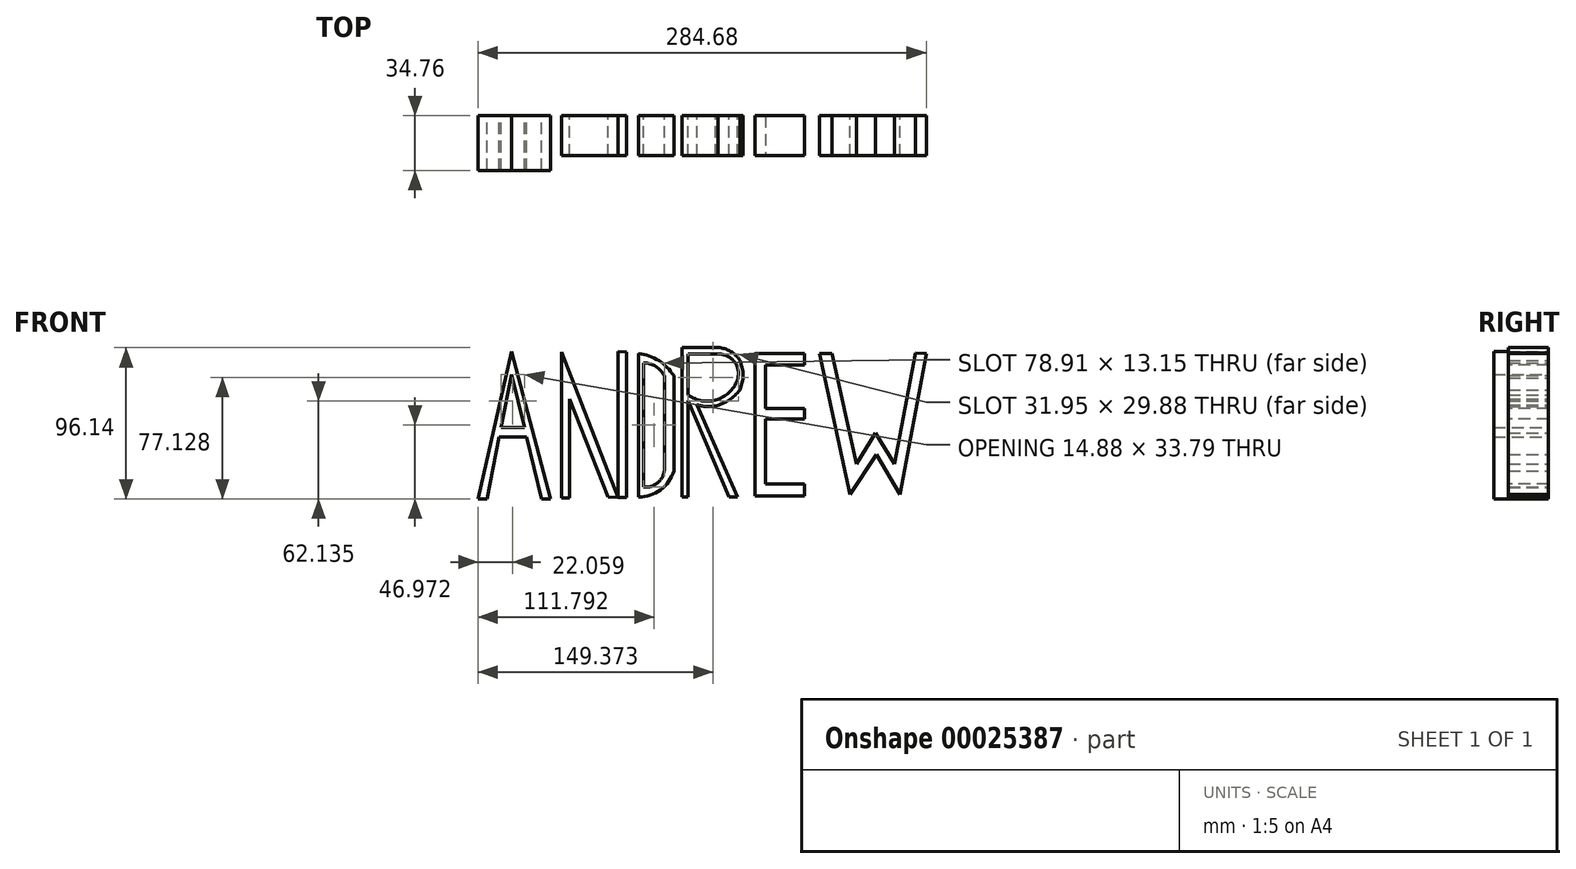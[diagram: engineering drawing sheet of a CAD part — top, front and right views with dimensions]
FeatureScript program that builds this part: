
annotation { "Feature Type Name" : "Feature", "Feature Type Description" : "" }
export const myFeature = defineFeature(function(context is Context, id is Id, definition is map)
    precondition{}
    {
        {
            var Q0;
            Q0=qCreatedBy(makeId("Front.planeOp"),FACE);
            var sketch = newSketch(context, id + "F0", { "sketchPlane" : qUnion([Q0])});
            skLineSegment(sketch, "E0", {"start": v(-75.47, -35.86) * mm, "end": v(-35.39, 55.58) * mm});
            skLineSegment(sketch, "E1", {"start": v(-68.9, -35.86) * mm, "end": v(-75.47, -35.86) * mm});
            skLineSegment(sketch, "E2", {"start": v(-68.9, -35.86) * mm, "end": v(-36.05, 39.07) * mm});
            skLineSegment(sketch, "E3", {"start": v(-36.05, 39.07) * mm, "end": v(-9.08, -38.99) * mm});
            skLineSegment(sketch, "E4", {"start": v(-9.08, -38.99) * mm, "end": v(-3.44, -38.99) * mm});
            skLineSegment(sketch, "E5", {"start": v(-3.44, -38.99) * mm, "end": v(-35.39, 55.58) * mm});
            skLineSegment(sketch, "E6", {"start": v(-53.18, 0) * mm, "end": v(-22.55, 0) * mm});
            skLineSegment(sketch, "E7", {"start": v(-49.54, 8.29) * mm, "end": v(-25.41, 8.29) * mm});
            skSolve(sketch);
        }
        {
            var Q0;
            {var subQ1=sQuery(id+"F0.wireOp",EDGE,"E6");Q0=makeQuery(id+"F0.imprint","IMPRINT",FACE,{"disambiguationData":[TD([[makeQuery(id+"F0.imprint","IMPRINT",EDGE,{"derivedFrom":subQ1}),1.0]])]});}
            var Q1;
            Q1=makeQuery(id+"F0.imprint","IMPRINT",FACE,{"disambiguationData":[TD([[makeQuery(id+"F0.imprint","IMPRINT",EDGE,{"derivedFrom":sQuery(id+"F0.wireOp",EDGE,"E0")}),-1.0]])]});
            extrude(context, id + "F1", {"entities" : qUnion([Q0, Q1]), "depth" : 25.4 * mm});
        }
        {
            var Q0;
            Q0=makeQuery(id+"F1.opExtrude","CAP_FACE",FACE,{"disambiguationData":[OSD([sQuery(id+"F0.wireOp",EDGE,"E0"),sQuery(id+"F0.wireOp",EDGE,"E1"),sQuery(id+"F0.wireOp",EDGE,"E2"),sQuery(id+"F0.wireOp",EDGE,"E3"),sQuery(id+"F0.wireOp",EDGE,"E4"),sQuery(id+"F0.wireOp",EDGE,"E5"),sQuery(id+"F0.wireOp",EDGE,"E6"),sQuery(id+"F0.wireOp",EDGE,"E7")])],"isStart":false});
            var sketch = newSketch(context, id + "F2", { "sketchPlane" : qUnion([Q0])});
            skSolve(sketch);
        }
        {
            var Q0;
            Q0 = qSketchRegion(id + "FRlJwE8yTnHYSPP_1", true);
            var Q1;
            Q1=makeQuery(id+"F2.imprint","IMPRINT",FACE,{"disambiguationData":[TD([[makeQuery(id+"F2.imprint","IMPRINT",EDGE,{"derivedFrom":makeQuery(id+"F1.opExtrude","CAP_EDGE",EDGE,{"disambiguationData":[OSD([sQuery(id+"F0.wireOp",EDGE,"E0")])],"isStart":false})}),-1.0]])]});
            extrude(context, id + "F3", {"entities" : qUnion([Q0, Q1]), "operationType" : NewBodyOperationType.ADD, "depth" : 25.4 * mm});
        }
        {
            var Q0;
            Q0=makeQuery(id+"F1.opExtrude","SWEPT_BODY",BODY,{"disambiguationData":[OSD([sQuery(id+"F0.wireOp",EDGE,"E0"),sQuery(id+"F0.wireOp",EDGE,"E1"),sQuery(id+"F0.wireOp",EDGE,"E2"),sQuery(id+"F0.wireOp",EDGE,"E3"),sQuery(id+"F0.wireOp",EDGE,"E4"),sQuery(id+"F0.wireOp",EDGE,"E5"),sQuery(id+"F0.wireOp",EDGE,"E6"),sQuery(id+"F0.wireOp",EDGE,"E7")])]});
            deleteBodies(context, id + "F4", {"entities" : qUnion([Q0])});
        }
        {
            var Q0;
            Q0=qCreatedBy(makeId("Front.planeOp"),FACE);
            var sketch = newSketch(context, id + "F5", { "sketchPlane" : qUnion([Q0])});
            skLineSegment(sketch, "E8", {"start": v(-74.84, -28.34) * mm, "end": v(-69.2, -28.34) * mm});
            skLineSegment(sketch, "E9", {"start": v(-74.84, -28.34) * mm, "end": v(-53.52, 65.43) * mm});
            skLineSegment(sketch, "E10", {"start": v(-53.52, 65.43) * mm, "end": v(-28.74, -28.34) * mm});
            skLineSegment(sketch, "E11", {"start": v(-69.2, -28.34) * mm, "end": v(-61.36, 11.17) * mm});
            skLineSegment(sketch, "E12", {"start": v(-53.52, 50.69) * mm, "end": v(-45.34, 16.9) * mm});
            skLineSegment(sketch, "E13", {"start": v(-61.36, 11.17) * mm, "end": v(-43.95, 11.17) * mm});
            skLineSegment(sketch, "E14", {"start": v(-60.22, 16.9) * mm, "end": v(-45.34, 16.9) * mm});
            skLineSegment(sketch, "E15.trimOffspring", {"start": v(-34.39, -28.34) * mm, "end": v(-28.74, -28.34) * mm});
            skLineSegment(sketch, "E16.trimOffspring", {"start": v(-60.22, 16.9) * mm, "end": v(-53.52, 50.69) * mm});
            skLineSegment(sketch, "E17.trimOffspring", {"start": v(-43.95, 11.17) * mm, "end": v(-34.39, -28.34) * mm});
            skSolve(sketch);
        }
        {
            var Q0;
            Q0=makeQuery(id+"F5.imprint","IMPRINT",FACE,{"disambiguationData":[TD([[makeQuery(id+"F5.imprint","IMPRINT",EDGE,{"derivedFrom":sQuery(id+"F5.wireOp",EDGE,"E8")}),1.0]])]});
            extrude(context, id + "F6", {"entities" : qUnion([Q0]), "depth" : 9.36 * mm});
        }
        {
            var Q0;
            Q0=qCreatedBy(makeId("Front.planeOp"),FACE);
            var sketch = newSketch(context, id + "F7", { "sketchPlane" : qUnion([Q0])});
            skLineSegment(sketch, "E18", {"start": v(-21.92, -27.71) * mm, "end": v(-21.92, 64.98) * mm});
            skLineSegment(sketch, "E19", {"start": v(-21.92, 64.98) * mm, "end": v(14.1, -27.4) * mm});
            skLineSegment(sketch, "E20", {"start": v(14.1, -27.4) * mm, "end": v(14.1, 65.3) * mm});
            skLineSegment(sketch, "E21", {"start": v(-21.92, -27.71) * mm, "end": v(-16.6, -27.71) * mm});
            skLineSegment(sketch, "E22", {"start": v(-16.6, -27.71) * mm, "end": v(-16.6, 35.23) * mm});
            skLineSegment(sketch, "E23", {"start": v(-16.6, 35.23) * mm, "end": v(7.73, -27.18) * mm});
            skLineSegment(sketch, "E24", {"start": v(7.73, -27.18) * mm, "end": v(14.1, -27.4) * mm});
            skLineSegment(sketch, "E25", {"start": v(14.1, -27.4) * mm, "end": v(19.42, -27.4) * mm});
            skLineSegment(sketch, "E26", {"start": v(19.42, -27.4) * mm, "end": v(19.42, 64.98) * mm});
            skLineSegment(sketch, "E27", {"start": v(19.42, 64.98) * mm, "end": v(14.1, 65.3) * mm});
            skSolve(sketch);
        }
        {
            var Q0;
            Q0=makeQuery(id+"F7.imprint","IMPRINT",FACE,{"disambiguationData":[TD([[makeQuery(id+"F7.imprint","IMPRINT",EDGE,{"derivedFrom":sQuery(id+"F7.wireOp",EDGE,"E20")}),-1.0]])]});
            var Q1;
            Q1=makeQuery(id+"F7.imprint","IMPRINT",FACE,{"disambiguationData":[TD([[makeQuery(id+"F7.imprint","IMPRINT",EDGE,{"derivedFrom":sQuery(id+"F7.wireOp",EDGE,"E18")}),-1.0]])]});
            extrude(context, id + "F8", {"entities" : qUnion([Q0, Q1]), "depth" : 25.4 * mm});
        }
        {
            var Q0;
            Q0=makeQuery(id+"F6.opExtrude","CAP_FACE",FACE,{"disambiguationData":[OSD([sQuery(id+"F5.wireOp",EDGE,"E8"),sQuery(id+"F5.wireOp",EDGE,"E9"),sQuery(id+"F5.wireOp",EDGE,"E10"),sQuery(id+"F5.wireOp",EDGE,"E11"),sQuery(id+"F5.wireOp",EDGE,"E12"),sQuery(id+"F5.wireOp",EDGE,"E13"),sQuery(id+"F5.wireOp",EDGE,"E14"),sQuery(id+"F5.wireOp",EDGE,"E15.trimOffspring"),sQuery(id+"F5.wireOp",EDGE,"E16.trimOffspring"),sQuery(id+"F5.wireOp",EDGE,"E17.trimOffspring")])],"isStart":false});
            extrude(context, id + "F9", {"entities" : qUnion([Q0]), "operationType" : NewBodyOperationType.ADD, "depth" : 25.4 * mm});
        }
        {
            var Q0;
            Q0=qCreatedBy(makeId("Front.planeOp"),FACE);
            var sketch = newSketch(context, id + "F10", { "sketchPlane" : qUnion([Q0])});
            skLineSegment(sketch, "E28", {"start": v(19.1, -27.09) * mm, "end": v(27.24, -27.09) * mm});
            skLineSegment(sketch, "E29", {"start": v(27.24, -27.09) * mm, "end": v(27.24, 64.04) * mm});
            skArc(sketch, "E30", {"start": v(49.48, 49.95) * mm, "mid": v(39.96, 59.52) * mm, "end": v(27.24, 64.04) * mm});
            skLineSegment(sketch, "E31", {"start": v(49.48, 49.95) * mm, "end": v(49.48, -10.5) * mm});
            skArc(sketch, "E32", {"start": v(27.24, -27.09) * mm, "mid": v(41.12, -22.48) * mm, "end": v(49.48, -10.5) * mm});
            skArc(sketch, "E33", {"start": v(43.53, 49.95) * mm, "mid": v(38.07, 55.83) * mm, "end": v(30.38, 58.09) * mm});
            skLineSegment(sketch, "E34", {"start": v(43.53, 49.95) * mm, "end": v(43.53, -8.92) * mm});
            skLineSegment(sketch, "E35", {"start": v(30.38, 58.09) * mm, "end": v(30.38, -8.92) * mm});
            skArc(sketch, "E36", {"start": v(30.38, -20.82) * mm, "mid": v(39.6, -17.8) * mm, "end": v(43.53, -8.92) * mm});
            skLineSegment(sketch, "E37", {"start": v(30.38, -20.82) * mm, "end": v(30.38, -8.92) * mm});
            skSolve(sketch);
        }
        {
            var Q0;
            Q0 = qSketchRegion(id + "F10", true);
            extrude(context, id + "F11", {"entities" : qUnion([Q0]), "depth" : 25.4 * mm});
        }
        {
            var Q0;
            Q0=qCreatedBy(makeId("Front.planeOp"),FACE);
            var sketch = newSketch(context, id + "F12", { "sketchPlane" : qUnion([Q0])});
            skLineSegment(sketch, "E38", {"start": v(58.56, -27.09) * mm, "end": v(58.56, 61.53) * mm});
            skLineSegment(sketch, "E39", {"start": v(58.56, 63.73) * mm, "end": v(58.56, 61.53) * mm});
            skLineSegment(sketch, "E40", {"start": v(58.56, 63.73) * mm, "end": v(77.97, 63.73) * mm});
            skArc(sketch, "E41", {"start": v(90.19, 48.38) * mm, "mid": v(87.78, 59) * mm, "end": v(77.97, 63.73) * mm});
            skArc(sketch, "E42", {"start": v(58.56, 37.73) * mm, "mid": v(77.14, 34.84) * mm, "end": v(90.19, 48.38) * mm});
            skArc(sketch, "E43", {"start": v(91.44, 59.66) * mm, "mid": v(85.55, 65.41) * mm, "end": v(77.66, 67.8) * mm});
            skArc(sketch, "E44", {"start": v(91.44, 40.87) * mm, "mid": v(93.42, 50.26) * mm, "end": v(91.44, 59.66) * mm});
            skArc(sketch, "E45", {"start": v(76.1, 30.85) * mm, "mid": v(84.63, 34.53) * mm, "end": v(91.44, 40.87) * mm});
            skArc(sketch, "E46", {"start": v(58.56, 34.3) * mm, "mid": v(66.97, 30.75) * mm, "end": v(76.1, 30.85) * mm});
            skLineSegment(sketch, "E47", {"start": v(77.66, 67.8) * mm, "end": v(58.56, 67.8) * mm});
            skLineSegment(sketch, "E48", {"start": v(58.56, 67.8) * mm, "end": v(58.56, 63.73) * mm});
            skLineSegment(sketch, "E49", {"start": v(58.56, 67.8) * mm, "end": v(54.8, 67.8) * mm});
            skLineSegment(sketch, "E50", {"start": v(54.8, 67.8) * mm, "end": v(54.8, -27.09) * mm});
            skLineSegment(sketch, "E51", {"start": v(54.8, -27.09) * mm, "end": v(58.56, -27.09) * mm});
            skLineSegment(sketch, "E52", {"start": v(58.56, 34.3) * mm, "end": v(84.55, -27.09) * mm});
            skLineSegment(sketch, "E53", {"start": v(84.55, -27.09) * mm, "end": v(89.87, -27.09) * mm});
            skLineSegment(sketch, "E54", {"start": v(89.87, -27.09) * mm, "end": v(64.16, 31.5) * mm});
            skSolve(sketch);
        }
        {
            var Q0;
            Q0 = qSketchRegion(id + "F12", true);
            extrude(context, id + "F13", {"entities" : qUnion([Q0]), "depth" : 25.4 * mm});
        }
        {
            var Q0;
            Q0=makeQuery(id+"F11.opExtrude","CAP_FACE",FACE,{"disambiguationData":[OSD([sQuery(id+"F10.wireOp",EDGE,"E29"),sQuery(id+"F10.wireOp",EDGE,"E30"),sQuery(id+"F10.wireOp",EDGE,"E31"),sQuery(id+"F10.wireOp",EDGE,"E32"),sQuery(id+"F10.wireOp",EDGE,"E33"),sQuery(id+"F10.wireOp",EDGE,"E34"),sQuery(id+"F10.wireOp",EDGE,"E35"),sQuery(id+"F10.wireOp",EDGE,"E36"),sQuery(id+"F10.wireOp",EDGE,"E37")])],"isStart":false});
            var sketch = newSketch(context, id + "F14", { "sketchPlane" : qUnion([Q0])});
            skLineSegment(sketch, "E55", {"start": v(132.62, 64.04) * mm, "end": v(101, 64.1) * mm});
            skLineSegment(sketch, "E56", {"start": v(101, 64.1) * mm, "end": v(101, -26.46) * mm});
            skLineSegment(sketch, "E57", {"start": v(132.62, 64.04) * mm, "end": v(132.62, 56.84) * mm});
            skLineSegment(sketch, "E58", {"start": v(132.62, 56.84) * mm, "end": v(107.88, 56.84) * mm});
            skLineSegment(sketch, "E59", {"start": v(107.88, 56.84) * mm, "end": v(107.88, 29.28) * mm});
            skLineSegment(sketch, "E60", {"start": v(107.88, 29.28) * mm, "end": v(132.62, 29.28) * mm});
            skLineSegment(sketch, "E61", {"start": v(132.62, 29.28) * mm, "end": v(132.62, 22.4) * mm});
            skLineSegment(sketch, "E62", {"start": v(132.62, 22.4) * mm, "end": v(107.88, 22.4) * mm});
            skLineSegment(sketch, "E63", {"start": v(107.88, 22.4) * mm, "end": v(107.88, -18.95) * mm});
            skLineSegment(sketch, "E64", {"start": v(107.88, -18.95) * mm, "end": v(132.62, -18.95) * mm});
            skLineSegment(sketch, "E65", {"start": v(132.62, -18.95) * mm, "end": v(132.62, -26.46) * mm});
            skLineSegment(sketch, "E66", {"start": v(132.62, -26.46) * mm, "end": v(101, -26.46) * mm});
            skSolve(sketch);
        }
        {
            var Q0;
            Q0=makeQuery(id+"F14.imprint","IMPRINT",FACE,{"disambiguationData":[TD([[makeQuery(id+"F14.imprint","IMPRINT",EDGE,{"derivedFrom":sQuery(id+"F14.wireOp",EDGE,"E55")}),1.0]])]});
            extrude(context, id + "F15", {"entities" : qUnion([Q0]), "oppositeDirection" : true, "depth" : 25.4 * mm});
        }
        {
            var Q0;
            Q0=qCreatedBy(makeId("Front.planeOp"),FACE);
            var sketch = newSketch(context, id + "F16", { "sketchPlane" : qUnion([Q0])});
            skLineSegment(sketch, "E67", {"start": v(141.88, 64.04) * mm, "end": v(161.3, -25.52) * mm});
            skLineSegment(sketch, "E68", {"start": v(141.88, 64.04) * mm, "end": v(150.03, 64.04) * mm});
            skLineSegment(sketch, "E69", {"start": v(150.03, 64.04) * mm, "end": v(165.37, -6.1) * mm});
            skLineSegment(sketch, "E70", {"start": v(161.3, -25.52) * mm, "end": v(178.2, 0) * mm});
            skLineSegment(sketch, "E71", {"start": v(178.2, 0) * mm, "end": v(193.24, -25.52) * mm});
            skLineSegment(sketch, "E72", {"start": v(193.24, -25.52) * mm, "end": v(209.84, 64.04) * mm});
            skLineSegment(sketch, "E73", {"start": v(189.8, -6.1) * mm, "end": v(202.87, 64.43) * mm});
            skLineSegment(sketch, "E74", {"start": v(202.87, 64.43) * mm, "end": v(209.84, 64.04) * mm});
            skLineSegment(sketch, "E75", {"start": v(165.37, -6.1) * mm, "end": v(177.58, 13.62) * mm});
            skLineSegment(sketch, "E76", {"start": v(177.58, 13.62) * mm, "end": v(189.8, -6.1) * mm});
            skSolve(sketch);
        }
        {
            var Q0;
            Q0=makeQuery(id+"F16.imprint","IMPRINT",FACE,{"disambiguationData":[TD([[makeQuery(id+"F16.imprint","IMPRINT",EDGE,{"derivedFrom":sQuery(id+"F16.wireOp",EDGE,"E67")}),1.0]])]});
            extrude(context, id + "F17", {"entities" : qUnion([Q0]), "depth" : 25.4 * mm});
        }
    });
